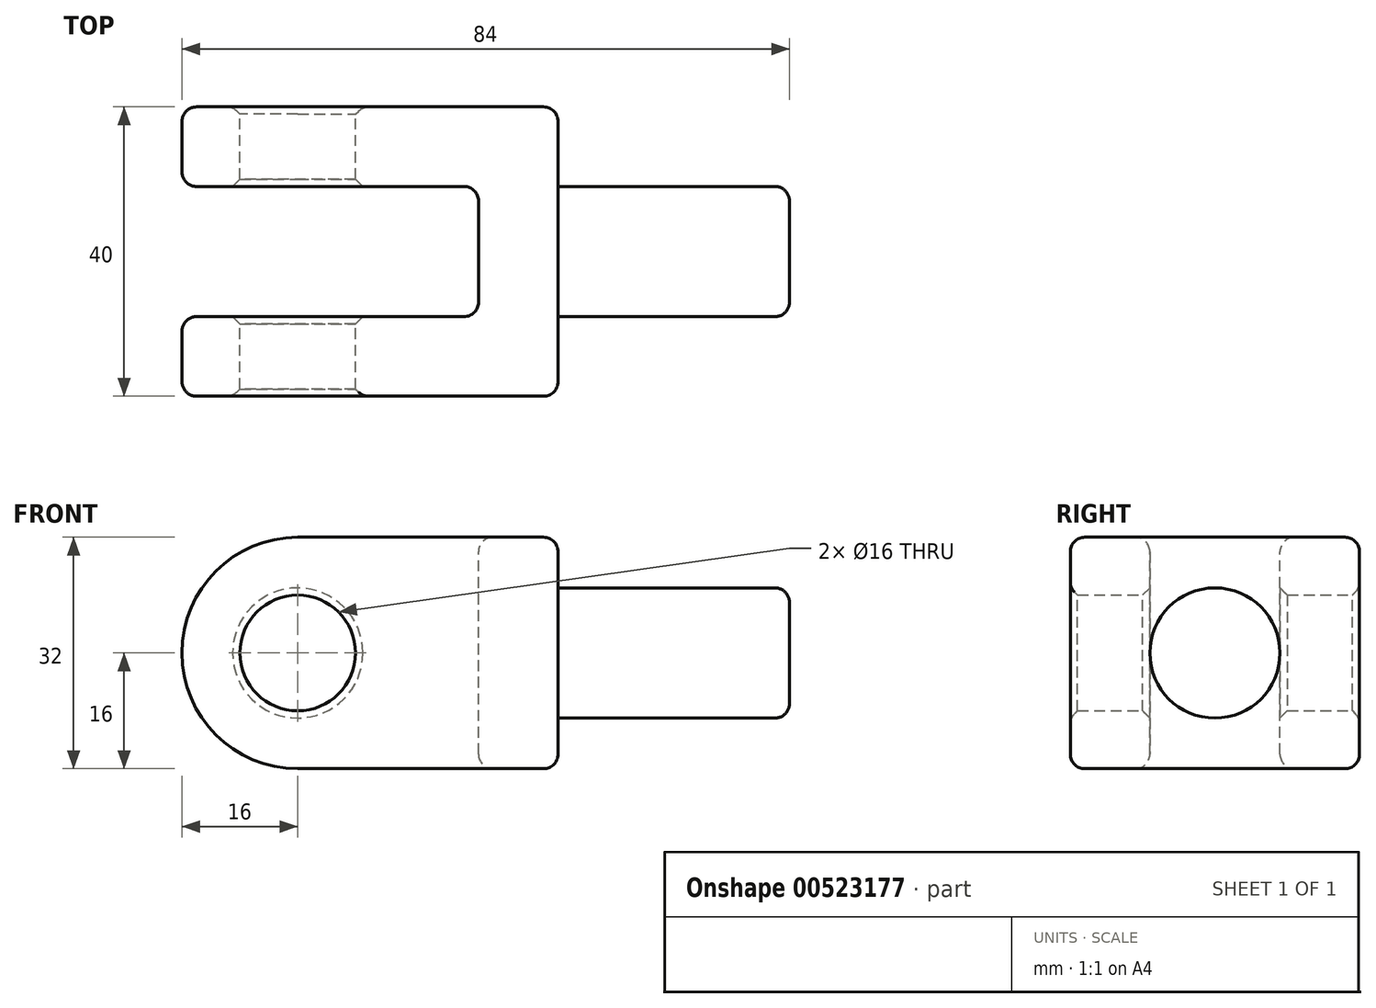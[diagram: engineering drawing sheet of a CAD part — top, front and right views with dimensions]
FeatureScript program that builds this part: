
annotation { "Feature Type Name" : "Feature", "Feature Type Description" : "" }
export const myFeature = defineFeature(function(context is Context, id is Id, definition is map)
    precondition{}
    {
        {
            var Q0;
            Q0=qCreatedBy(makeId("Front.planeOp"),FACE);
            var sketch = newSketch(context, id + "F0", { "sketchPlane" : qUnion([Q0])});
            skLineSegment(sketch, "E0", {"start": v(0, 0) * mm, "end": v(-36, 0) * mm});
            skLineSegment(sketch, "E1", {"start": v(0, 0) * mm, "end": v(0, 32) * mm});
            skLineSegment(sketch, "E2", {"start": v(0, 32) * mm, "end": v(-36, 32) * mm});
            skArc(sketch, "E3", {"start": v(-36, 32) * mm, "mid": v(-52, 16) * mm, "end": v(-36, 0) * mm});
            skCircle(sketch, "E4", {"center": v(-36, 16) * mm, "radius": 8 * mm});
            skSolve(sketch);
        }
        {
            var Q0;
            Q0=makeQuery(id+"F0.imprint","IMPRINT",FACE,{"disambiguationData":[TD([[makeQuery(id+"F0.imprint","IMPRINT",EDGE,{"derivedFrom":sQuery(id+"F0.wireOp",EDGE,"E0")}),-1.0]])]});
            extrude(context, id + "F1", {"entities" : qUnion([Q0]), "depth" : 40 * mm, "offsetDistance" : 25 * mm});
        }
        {
            var Q0;
            Q0=makeQuery(id+"F1.opExtrude","SWEPT_FACE",FACE,{"disambiguationData":[OSD([sQuery(id+"F0.wireOp",EDGE,"E2")])]});
            var sketch = newSketch(context, id + "F2", { "sketchPlane" : qUnion([Q0])});
            skLineSegment(sketch, "E5", {"start": v(0, 0) * mm, "end": v(-11, 0) * mm, "construction": true});
            skLineSegment(sketch, "E6", {"start": v(-11, 0) * mm, "end": v(-11, -11) * mm, "construction": true});
            skLineSegment(sketch, "E7", {"start": v(-11, -11) * mm, "end": v(-52, -11) * mm});
            skLineSegment(sketch, "E8", {"start": v(-52, -11) * mm, "end": v(-52, -29) * mm});
            skLineSegment(sketch, "E9", {"start": v(-52, -29) * mm, "end": v(-11, -29) * mm});
            skLineSegment(sketch, "E10", {"start": v(-11, -29) * mm, "end": v(-11, -11) * mm});
            skSolve(sketch);
        }
        {
            var Q0;
            {var subQ0=sQuery(id+"F2.wireOp",EDGE,"E10");Q0=makeQuery(id+"F2.imprint","IMPRINT",FACE,{"disambiguationData":[TD([[makeQuery(id+"F2.imprint","IMPRINT",EDGE,{"derivedFrom":subQ0}),1.0]])]});}
            var Q1;
            {var subQ0=sQuery(id+"F2.wireOp",EDGE,"E8");Q1=makeQuery(id+"F2.imprint","IMPRINT",FACE,{"disambiguationData":[TD([[makeQuery(id+"F2.imprint","IMPRINT",EDGE,{"derivedFrom":subQ0}),1.0]])]});}
            extrude(context, id + "F3", {"entities" : qUnion([Q0, Q1]), "operationType" : NewBodyOperationType.REMOVE, "endBound" : BoundingType.THROUGH_ALL, "oppositeDirection" : true, "depth" : 25 * mm, "offsetDistance" : 25 * mm});
        }
        {
            var Q0;
            Q0=makeQuery(id+"F1.opExtrude","SWEPT_FACE",FACE,{"disambiguationData":[OSD([sQuery(id+"F0.wireOp",EDGE,"E1")])]});
            var sketch = newSketch(context, id + "F4", { "sketchPlane" : qUnion([Q0])});
            skLineSegment(sketch, "E11", {"start": v(-40, 16) * mm, "end": v(0, 16) * mm, "construction": true});
            skLineSegment(sketch, "E12", {"start": v(-20, 0) * mm, "end": v(-20, 32) * mm, "construction": true});
            skCircle(sketch, "E13", {"center": v(-20, 16) * mm, "radius": 9 * mm});
            skSolve(sketch);
        }
        {
            var Q0;
            Q0 = qSketchRegion(id + "F4", true);
            extrude(context, id + "F5", {"entities" : qUnion([Q0]), "operationType" : NewBodyOperationType.ADD, "depth" : 32 * mm, "offsetDistance" : 25 * mm});
        }
        {
            var Q0;
            Q0=makeQuery(id+"F1.opExtrude","CAP_EDGE",EDGE,{"disambiguationData":[OSD([sQuery(id+"F0.wireOp",EDGE,"E4")])],"isStart":false});
            var Q1;
            Q1=makeQuery(id+"F3.boolean.opBoolean","INTERSECT",EDGE,{"derivedFrom":[makeQuery(id+"F1.opExtrude","SWEPT_FACE",FACE,{"disambiguationData":[OSD([sQuery(id+"F0.wireOp",EDGE,"E4")])]}),makeQuery(id+"F3.opExtrude","SWEPT_FACE",FACE,{"disambiguationData":[OSD([sQuery(id+"F2.wireOp",EDGE,"E9")])]})]});
            var Q2;
            Q2=makeQuery(id+"F3.boolean.opBoolean","INTERSECT",EDGE,{"derivedFrom":[makeQuery(id+"F1.opExtrude","SWEPT_FACE",FACE,{"disambiguationData":[OSD([sQuery(id+"F0.wireOp",EDGE,"E4")])]}),makeQuery(id+"F3.opExtrude","SWEPT_FACE",FACE,{"disambiguationData":[OSD([sQuery(id+"F2.wireOp",EDGE,"E7")])]})]});
            var Q3;
            Q3=makeQuery(id+"F1.opExtrude","CAP_EDGE",EDGE,{"disambiguationData":[OSD([sQuery(id+"F0.wireOp",EDGE,"E4")])],"isStart":true});
            chamfer(context, id + "F6", {"entities" : qUnion([Q0, Q1, Q2, Q3]), "chamferType" : ChamferType.OFFSET_ANGLE, "width" : 1 * mm, "oppositeDirection" : false, "angle" : 45 * degree, "tangentPropagation" : true});
        }
        {
            var Q0;
            Q0=makeQuery(id+"F1.opExtrude","SWEPT_FACE",FACE,{"disambiguationData":[OSD([sQuery(id+"F0.wireOp",EDGE,"E2")])]});
            var Q1;
            Q1=makeQuery(id+"F1.opExtrude","CAP_FACE",FACE,{"disambiguationData":[OSD([sQuery(id+"F0.wireOp",EDGE,"E0"),sQuery(id+"F0.wireOp",EDGE,"E1"),sQuery(id+"F0.wireOp",EDGE,"E2"),sQuery(id+"F0.wireOp",EDGE,"E3"),sQuery(id+"F0.wireOp",EDGE,"E4")])],"isStart":false});
            var Q2;
            Q2=makeQuery(id+"F1.opExtrude","CAP_FACE",FACE,{"disambiguationData":[OSD([sQuery(id+"F0.wireOp",EDGE,"E0"),sQuery(id+"F0.wireOp",EDGE,"E1"),sQuery(id+"F0.wireOp",EDGE,"E2"),sQuery(id+"F0.wireOp",EDGE,"E3"),sQuery(id+"F0.wireOp",EDGE,"E4")])],"isStart":true});
            var Q3;
            Q3=makeQuery(id+"F1.opExtrude","SWEPT_FACE",FACE,{"disambiguationData":[OSD([sQuery(id+"F0.wireOp",EDGE,"E0")])]});
            var Q4;
            Q4=makeQuery(id+"F5.opExtrude","CAP_FACE",FACE,{"disambiguationData":[OSD([sQuery(id+"F4.wireOp",EDGE,"E13")])],"isStart":false});
            var Q5;
            Q5=makeQuery(id+"F5.opExtrude","CAP_EDGE",EDGE,{"disambiguationData":[OSD([sQuery(id+"F4.wireOp",EDGE,"E13")])],"isStart":true});
            var Q6;
            Q6=makeQuery(id+"F3.boolean.opBoolean","COPY",FACE,{"derivedFrom":makeQuery(id+"F3.opExtrude","SWEPT_FACE",FACE,{"disambiguationData":[OSD([sQuery(id+"F2.wireOp",EDGE,"E10")])]})});
            fillet(context, id + "F7", {"entities" : qUnion([Q0, Q1, Q2, Q3, Q4, Q5, Q6]), "radius" : 2 * mm, "tangentPropagation" : true, "allowEdgeOverflow" : false});
        }
    });
